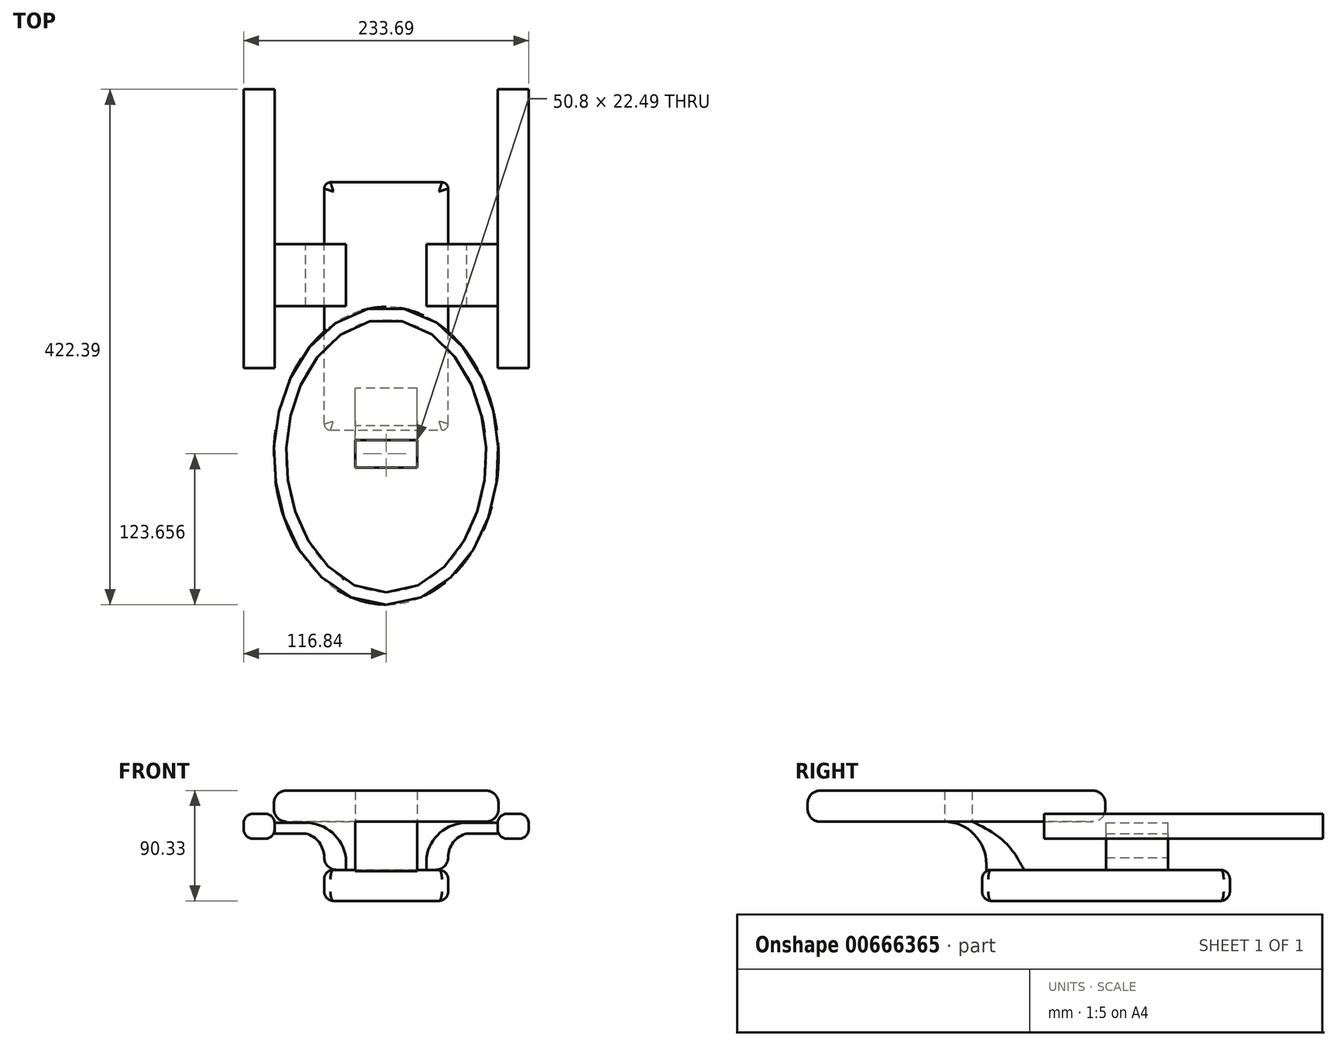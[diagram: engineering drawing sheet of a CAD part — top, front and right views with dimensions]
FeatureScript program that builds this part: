
annotation { "Feature Type Name" : "Feature", "Feature Type Description" : "" }
export const myFeature = defineFeature(function(context is Context, id is Id, definition is map)
    precondition{}
    {
        {
            var Q0;
            Q0=qCreatedBy(makeId("Front.planeOp"),FACE);
            var sketch = newSketch(context, id + "F0", { "sketchPlane" : qUnion([Q0])});
            skLineSegment(sketch, "E0.bottom", {"start": v(-50.8, 12.7) * mm, "end": v(50.8, 12.7) * mm});
            skLineSegment(sketch, "E0.top", {"start": v(-50.8, -12.7) * mm, "end": v(50.8, -12.7) * mm});
            skLineSegment(sketch, "E0.left", {"start": v(-50.8, 12.7) * mm, "end": v(-50.8, -12.7) * mm});
            skLineSegment(sketch, "E0.right", {"start": v(50.8, 12.7) * mm, "end": v(50.8, -12.7) * mm});
            skPoint(sketch, "E0.middle", {"position": v(0, 0) * mm});
            skLineSegment(sketch, "E1.bottom", {"start": v(-91.44, 38.28) * mm, "end": v(-116.84, 38.28) * mm});
            skLineSegment(sketch, "E1.top", {"start": v(-91.44, 58.6) * mm, "end": v(-116.84, 58.6) * mm});
            skLineSegment(sketch, "E1.left", {"start": v(-91.44, 38.28) * mm, "end": v(-91.44, 58.6) * mm});
            skLineSegment(sketch, "E1.right", {"start": v(-116.84, 38.28) * mm, "end": v(-116.84, 58.6) * mm});
            skPoint(sketch, "E1.middle", {"position": v(-104.14, 48.44) * mm});
            skLineSegment(sketch, "E2.bottom", {"start": v(91.45, 38.28) * mm, "end": v(116.85, 38.28) * mm});
            skLineSegment(sketch, "E2.top", {"start": v(91.45, 58.6) * mm, "end": v(116.85, 58.6) * mm});
            skLineSegment(sketch, "E2.left", {"start": v(91.45, 38.28) * mm, "end": v(91.45, 58.6) * mm});
            skLineSegment(sketch, "E2.right", {"start": v(116.85, 38.28) * mm, "end": v(116.85, 58.6) * mm});
            skPoint(sketch, "E2.middle", {"position": v(104.15, 48.44) * mm});
            skPoint(sketch, "E2.middle.positionSnap0", {"position": v(-91.44, 48.44) * mm});
            skPoint(sketch, "E2.centerSnap0", {"position": v(-91.44, 48.44) * mm});
            skLineSegment(sketch, "E3", {"start": v(50.8, 12.7) * mm, "end": v(50.8, 22.86) * mm});
            skLineSegment(sketch, "E4", {"start": v(-50.8, 12.7) * mm, "end": v(-50.8, 22.86) * mm});
            skArc(sketch, "E5", {"start": v(50.8, 22.86) * mm, "mid": v(55.06, 35.3) * mm, "end": v(66.05, 42.5) * mm});
            skLineSegment(sketch, "E6", {"start": v(66.05, 42.5) * mm, "end": v(91.45, 42.5) * mm});
            skArc(sketch, "E7", {"start": v(-50.8, 22.86) * mm, "mid": v(-55.06, 35.29) * mm, "end": v(-66.04, 42.5) * mm});
            skLineSegment(sketch, "E8", {"start": v(-66.04, 42.5) * mm, "end": v(-91.44, 42.38) * mm});
            skLineSegment(sketch, "E9", {"start": v(91.45, 51.35) * mm, "end": v(66.05, 51.35) * mm});
            skArc(sketch, "E10", {"start": v(66.05, 51.35) * mm, "mid": v(44.24, 43.24) * mm, "end": v(33.02, 22.86) * mm});
            skLineSegment(sketch, "E11", {"start": v(33.02, 22.86) * mm, "end": v(33.02, 12.7) * mm});
            skLineSegment(sketch, "E12", {"start": v(-91.44, 51.35) * mm, "end": v(-66.04, 51.35) * mm});
            skArc(sketch, "E13", {"start": v(-66.04, 51.35) * mm, "mid": v(-44.23, 43.24) * mm, "end": v(-33.02, 22.86) * mm});
            skLineSegment(sketch, "E14", {"start": v(-33.02, 22.86) * mm, "end": v(-33.02, 12.7) * mm});
            skSolve(sketch);
        }
        {
            var Q0;
            Q0=makeQuery(id+"F0.imprint","IMPRINT",FACE,{"disambiguationData":[TD([[makeQuery(id+"F0.imprint","IMPRINT",EDGE,{"derivedFrom":sQuery(id+"F0.wireOp",EDGE,"E0.top")}),1.0]])]});
            extrude(context, id + "F1", {"entities" : qUnion([Q0]), "depth" : 127 * mm, "offsetDistance" : 25.4 * mm, "hasSecondDirection" : true, "secondDirectionOppositeDirection" : true, "secondDirectionDepth" : 76.2 * mm});
        }
        {
            var Q0;
            {var subQ3=sQuery(id+"F0.wireOp",EDGE,"E2.bottom");Q0=makeQuery(id+"F0.imprint","IMPRINT",FACE,{"disambiguationData":[TD([[makeQuery(id+"F0.imprint","IMPRINT",EDGE,{"derivedFrom":subQ3}),1.0]])]});}
            extrude(context, id + "F2", {"entities" : qUnion([Q0]), "depth" : 76.2 * mm, "offsetDistance" : 25.4 * mm, "hasSecondDirection" : true, "secondDirectionOppositeDirection" : true, "secondDirectionDepth" : 152.4 * mm});
        }
        {
            var Q0;
            {var subQ3=sQuery(id+"F0.wireOp",EDGE,"E1.bottom");Q0=makeQuery(id+"F0.imprint","IMPRINT",FACE,{"disambiguationData":[TD([[makeQuery(id+"F0.imprint","IMPRINT",EDGE,{"derivedFrom":subQ3}),-1.0]])]});}
            extrude(context, id + "F3", {"entities" : qUnion([Q0]), "depth" : 76.2 * mm, "offsetDistance" : 25.4 * mm, "hasSecondDirection" : true, "secondDirectionOppositeDirection" : true, "secondDirectionDepth" : 152.4 * mm});
        }
        {
            var Q0;
            {var subQ0=sQuery(id+"F0.wireOp",EDGE,"E4");Q0=makeQuery(id+"F0.imprint","IMPRINT",FACE,{"disambiguationData":[TD([[makeQuery(id+"F0.imprint","IMPRINT",EDGE,{"derivedFrom":subQ0}),-1.0]])]});}
            extrude(context, id + "F4", {"entities" : qUnion([Q0]), "depth" : 25.4 * mm, "offsetDistance" : 25.4 * mm, "hasSecondDirection" : true, "secondDirectionOppositeDirection" : true, "secondDirectionDepth" : 25.4 * mm});
        }
        {
            var Q0;
            {var subQ0=sQuery(id+"F0.wireOp",EDGE,"E3");Q0=makeQuery(id+"F0.imprint","IMPRINT",FACE,{"disambiguationData":[TD([[makeQuery(id+"F0.imprint","IMPRINT",EDGE,{"derivedFrom":subQ0}),1.0]])]});}
            extrude(context, id + "F5", {"entities" : qUnion([Q0]), "depth" : 25.4 * mm, "offsetDistance" : 25.4 * mm, "hasSecondDirection" : true, "secondDirectionOppositeDirection" : true, "secondDirectionDepth" : 25.4 * mm});
        }
        {
            var Q0;
            Q0=qCreatedBy(makeId("Right.planeOp"),FACE);
            var sketch = newSketch(context, id + "F6", { "sketchPlane" : qUnion([Q0])});
            skLineSegment(sketch, "E15", {"start": v(-123.49, 12.39) * mm, "end": v(-123.49, 17.47) * mm});
            skArc(sketch, "E16", {"start": v(-123.49, 17.47) * mm, "mid": v(-133.92, 42.3) * mm, "end": v(-158.95, 52.23) * mm});
            skLineSegment(sketch, "E17", {"start": v(-158.95, 52.23) * mm, "end": v(-158.95, 62.4) * mm});
            skFitSpline(sketch, "E18", {"points": [v(-158.95, 62.4) * mm, v(-110.55, 37.49) * mm, v(-92.4, 12.39) * mm], "startDerivative": vector(97.08, -39.51) * mm, "endDerivative": vector(33.03, -61.53) * mm});
            skLineSegment(sketch, "E19", {"start": v(-123.49, 12.39) * mm, "end": v(-92.4, 12.39) * mm});
            skLineSegment(sketch, "E20.bottom", {"start": v(-240.74, 52.23) * mm, "end": v(-77.16, 52.23) * mm});
            skLineSegment(sketch, "E20.top", {"start": v(-240.74, 72.55) * mm, "end": v(-77.16, 72.55) * mm});
            skLineSegment(sketch, "E20.left", {"start": v(-240.74, 52.23) * mm, "end": v(-240.74, 72.55) * mm});
            skLineSegment(sketch, "E20.right", {"start": v(-77.16, 52.23) * mm, "end": v(-77.16, 72.55) * mm});
            skSolve(sketch);
        }
        {
            var Q0;
            {var subQ2=sQuery(id+"F6.wireOp",EDGE,"E15");Q0=makeQuery(id+"F6.imprint","IMPRINT",FACE,{"disambiguationData":[TD([[makeQuery(id+"F6.imprint","IMPRINT",EDGE,{"derivedFrom":subQ2}),-1.0]])]});}
            extrude(context, id + "F7", {"entities" : qUnion([Q0]), "operationType" : NewBodyOperationType.ADD, "depth" : 50.8 * mm, "offsetDistance" : 25.4 * mm, "symmetric" : true});
        }
        {
            var Q0;
            Q0=makeQuery(id+"F7.opExtrude","SWEPT_FACE",FACE,{"disambiguationData":[OSD([sQuery(id+"F6.wireOp",EDGE,"E20.bottom")])]});
            var sketch = newSketch(context, id + "F8", { "sketchPlane" : qUnion([Q0])});
            skEllipse(sketch, "E21", {"center": v(0, -147.96) * mm, "majorRadius": 122.03 * mm, "minorRadius": 92.08 * mm, "majorAxis": v(0, -1)});
            skPoint(sketch, "E21.centerSnap0", {"position": v(0, -157.58) * mm});
            skSolve(sketch);
        }
        {
            var Q0;
            Q0=makeQuery(id+"F8.imprint","IMPRINT",FACE,{"disambiguationData":[TD([[makeQuery(id+"F8.imprint","IMPRINT",EDGE,{"derivedFrom":sQuery(id+"F8.wireOp",EDGE,"E21")}),1.0]])]});
            extrude(context, id + "F9", {"entities" : qUnion([Q0]), "depth" : 25.4 * mm, "offsetDistance" : 25.4 * mm});
        }
        {
            var Q0;
            Q0=makeQuery(id+"F1.opExtrude","CAP_EDGE",EDGE,{"disambiguationData":[OSD([sQuery(id+"F0.wireOp",EDGE,"E0.right")])],"isStart":false});
            var Q1;
            Q1=makeQuery(id+"F1.opExtrude","CAP_EDGE",EDGE,{"disambiguationData":[OSD([sQuery(id+"F0.wireOp",EDGE,"E0.left")])],"isStart":false});
            var Q2;
            Q2=makeQuery(id+"F1.opExtrude","CAP_EDGE",EDGE,{"disambiguationData":[OSD([sQuery(id+"F0.wireOp",EDGE,"E0.right")])],"isStart":true});
            var Q3;
            Q3=makeQuery(id+"F1.opExtrude","CAP_EDGE",EDGE,{"disambiguationData":[OSD([sQuery(id+"F0.wireOp",EDGE,"E0.left")])],"isStart":true});
            fillet(context, id + "F10", {"entities" : qUnion([Q0, Q1, Q2, Q3]), "radius" : 5.08 * mm, "tangentPropagation" : true, "allowEdgeOverflow" : false});
        }
        {
            var Q0;
            Q0=makeQuery(id+"F1.opExtrude","SWEPT_EDGE",EDGE,{"disambiguationData":[OSD([sQuery(id+"F0.wireOp",EDGE,"E0.bottom"),sQuery(id+"F0.wireOp",EDGE,"E0.right"),sQuery(id+"F0.wireOp",EDGE,"E3")])]});
            var Q1;
            Q1=makeQuery(id+"F1.opExtrude","SWEPT_EDGE",EDGE,{"disambiguationData":[OSD([sQuery(id+"F0.wireOp",EDGE,"E0.top"),sQuery(id+"F0.wireOp",EDGE,"E0.right")])]});
            var Q2;
            Q2=makeQuery(id+"F1.opExtrude","SWEPT_EDGE",EDGE,{"disambiguationData":[OSD([sQuery(id+"F0.wireOp",EDGE,"E0.top"),sQuery(id+"F0.wireOp",EDGE,"E0.left")])]});
            var Q3;
            Q3=makeQuery(id+"F1.opExtrude","SWEPT_EDGE",EDGE,{"disambiguationData":[OSD([sQuery(id+"F0.wireOp",EDGE,"E0.bottom"),sQuery(id+"F0.wireOp",EDGE,"E0.left"),sQuery(id+"F0.wireOp",EDGE,"E4")])]});
            fillet(context, id + "F11", {"entities" : qUnion([Q0, Q1, Q2, Q3]), "radius" : 7.62 * mm, "tangentPropagation" : true, "allowEdgeOverflow" : false});
        }
        {
            var Q0;
            Q0=makeQuery(id+"F9.opExtrude","CAP_EDGE",EDGE,{"disambiguationData":[OSD([sQuery(id+"F8.wireOp",EDGE,"E21")])],"isStart":true});
            var Q1;
            Q1=makeQuery(id+"F9.opExtrude","CAP_EDGE",EDGE,{"disambiguationData":[OSD([sQuery(id+"F8.wireOp",EDGE,"E21")])],"isStart":false});
            fillet(context, id + "F12", {"entities" : qUnion([Q0, Q1]), "radius" : 10.16 * mm, "tangentPropagation" : true, "allowEdgeOverflow" : false});
        }
        {
            var Q0;
            Q0=makeQuery(id+"F2.opExtrude","SWEPT_EDGE",EDGE,{"disambiguationData":[OSD([sQuery(id+"F0.wireOp",EDGE,"E2.top"),sQuery(id+"F0.wireOp",EDGE,"E2.right")])]});
            var Q1;
            Q1=makeQuery(id+"F2.opExtrude","SWEPT_EDGE",EDGE,{"disambiguationData":[OSD([sQuery(id+"F0.wireOp",EDGE,"E2.top"),sQuery(id+"F0.wireOp",EDGE,"E2.left")])]});
            var Q2;
            Q2=makeQuery(id+"F2.opExtrude","SWEPT_EDGE",EDGE,{"disambiguationData":[OSD([sQuery(id+"F0.wireOp",EDGE,"E2.bottom"),sQuery(id+"F0.wireOp",EDGE,"E2.left")])]});
            var Q3;
            Q3=makeQuery(id+"F3.opExtrude","SWEPT_EDGE",EDGE,{"disambiguationData":[OSD([sQuery(id+"F0.wireOp",EDGE,"E1.top"),sQuery(id+"F0.wireOp",EDGE,"E1.left")])]});
            var Q4;
            Q4=makeQuery(id+"F3.opExtrude","SWEPT_EDGE",EDGE,{"disambiguationData":[OSD([sQuery(id+"F0.wireOp",EDGE,"E1.top"),sQuery(id+"F0.wireOp",EDGE,"E1.right")])]});
            var Q5;
            Q5=makeQuery(id+"F3.opExtrude","SWEPT_EDGE",EDGE,{"disambiguationData":[OSD([sQuery(id+"F0.wireOp",EDGE,"E1.bottom"),sQuery(id+"F0.wireOp",EDGE,"E1.right")])]});
            var Q6;
            Q6=makeQuery(id+"F3.opExtrude","SWEPT_EDGE",EDGE,{"disambiguationData":[OSD([sQuery(id+"F0.wireOp",EDGE,"E1.bottom"),sQuery(id+"F0.wireOp",EDGE,"E1.left")])]});
            var Q7;
            Q7=makeQuery(id+"F2.opExtrude","SWEPT_EDGE",EDGE,{"disambiguationData":[OSD([sQuery(id+"F0.wireOp",EDGE,"E2.bottom"),sQuery(id+"F0.wireOp",EDGE,"E2.right")])]});
            fillet(context, id + "F13", {"entities" : qUnion([Q0, Q1, Q2, Q3, Q4, Q5, Q6, Q7]), "radius" : 7.62 * mm, "tangentPropagation" : true, "allowEdgeOverflow" : false});
        }
        {
            var Q0;
            Q0=makeQuery(id+"F5.opExtrude","SWEPT_EDGE",EDGE,{"disambiguationData":[OSD([sQuery(id+"F0.wireOp",EDGE,"E0.bottom"),sQuery(id+"F0.wireOp",EDGE,"E0.right"),sQuery(id+"F0.wireOp",EDGE,"E3")])]});
            var Q1;
            Q1=makeQuery(id+"F4.opExtrude","SWEPT_EDGE",EDGE,{"disambiguationData":[OSD([sQuery(id+"F0.wireOp",EDGE,"E0.bottom"),sQuery(id+"F0.wireOp",EDGE,"E0.left"),sQuery(id+"F0.wireOp",EDGE,"E4")])]});
            fillet(context, id + "F14", {"entities" : qUnion([Q0, Q1]), "radius" : 10.16 * mm, "tangentPropagation" : true, "allowEdgeOverflow" : false});
        }
    });
